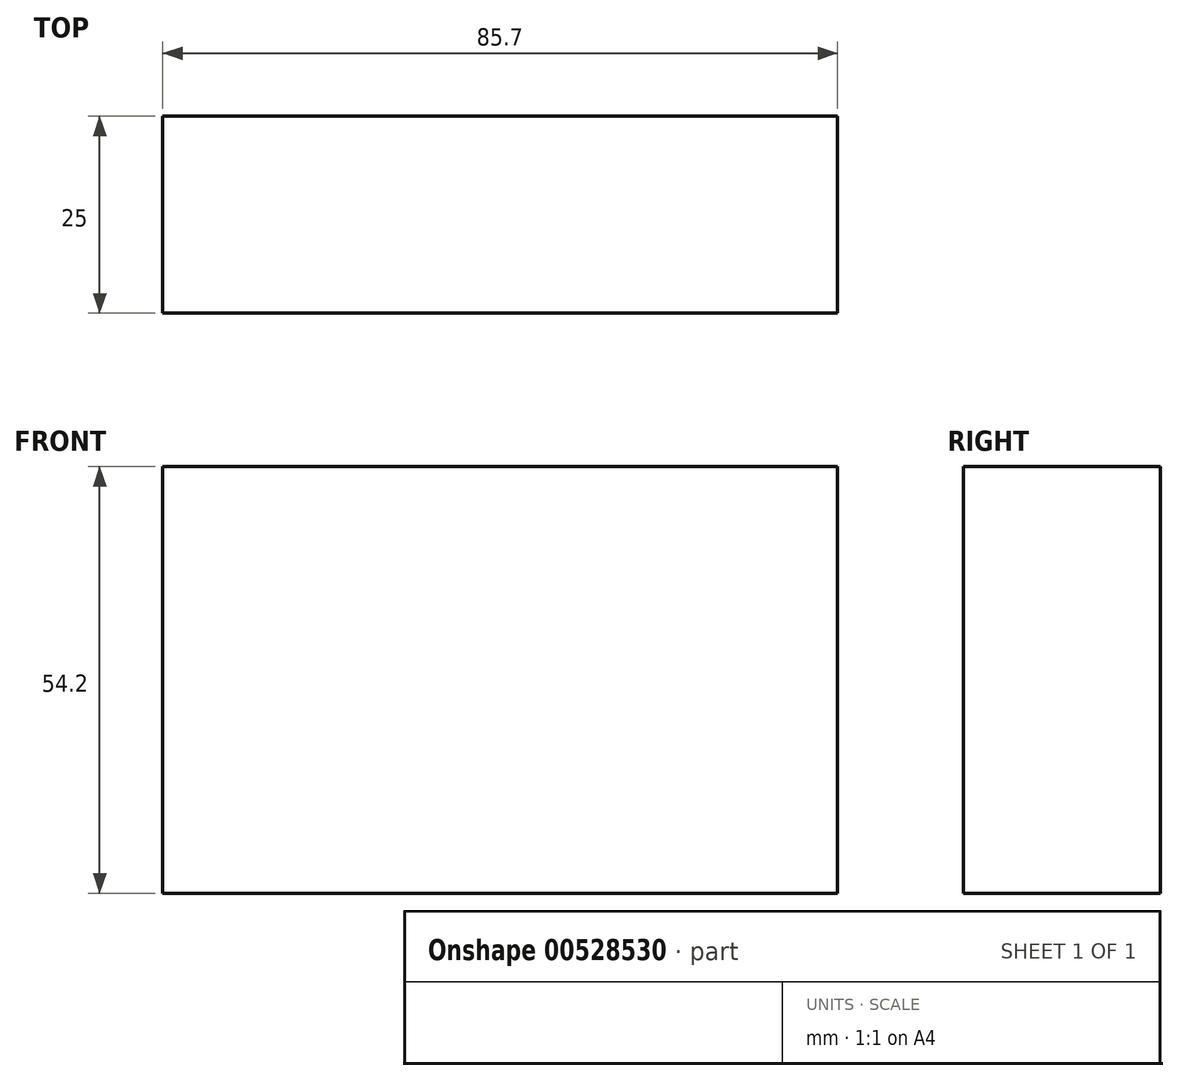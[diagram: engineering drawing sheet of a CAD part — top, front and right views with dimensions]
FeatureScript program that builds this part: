
annotation { "Feature Type Name" : "Feature", "Feature Type Description" : "" }
export const myFeature = defineFeature(function(context is Context, id is Id, definition is map)
    precondition{}
    {
        {
            var Q0;
            Q0=qCreatedBy(makeId("Front.planeOp"),FACE);
            var sketch = newSketch(context, id + "F0", { "sketchPlane" : qUnion([Q0])});
            skLineSegment(sketch, "E0.bottom", {"start": v(-42.85, 27.1) * mm, "end": v(42.85, 27.1) * mm});
            skLineSegment(sketch, "E0.top", {"start": v(-42.85, -27.1) * mm, "end": v(42.85, -27.1) * mm});
            skLineSegment(sketch, "E0.left", {"start": v(-42.85, 27.1) * mm, "end": v(-42.85, -27.1) * mm});
            skLineSegment(sketch, "E0.right", {"start": v(42.85, 27.1) * mm, "end": v(42.85, -27.1) * mm});
            skPoint(sketch, "E0.middle", {"position": v(0, 0) * mm});
            skSolve(sketch);
        }
        {
            var Q0;
            Q0 = qSketchRegion(id + "F0", true);
            extrude(context, id + "F1", {"entities" : qUnion([Q0]), "depth" : 25 * mm, "offsetDistance" : 25 * mm});
        }
    });
